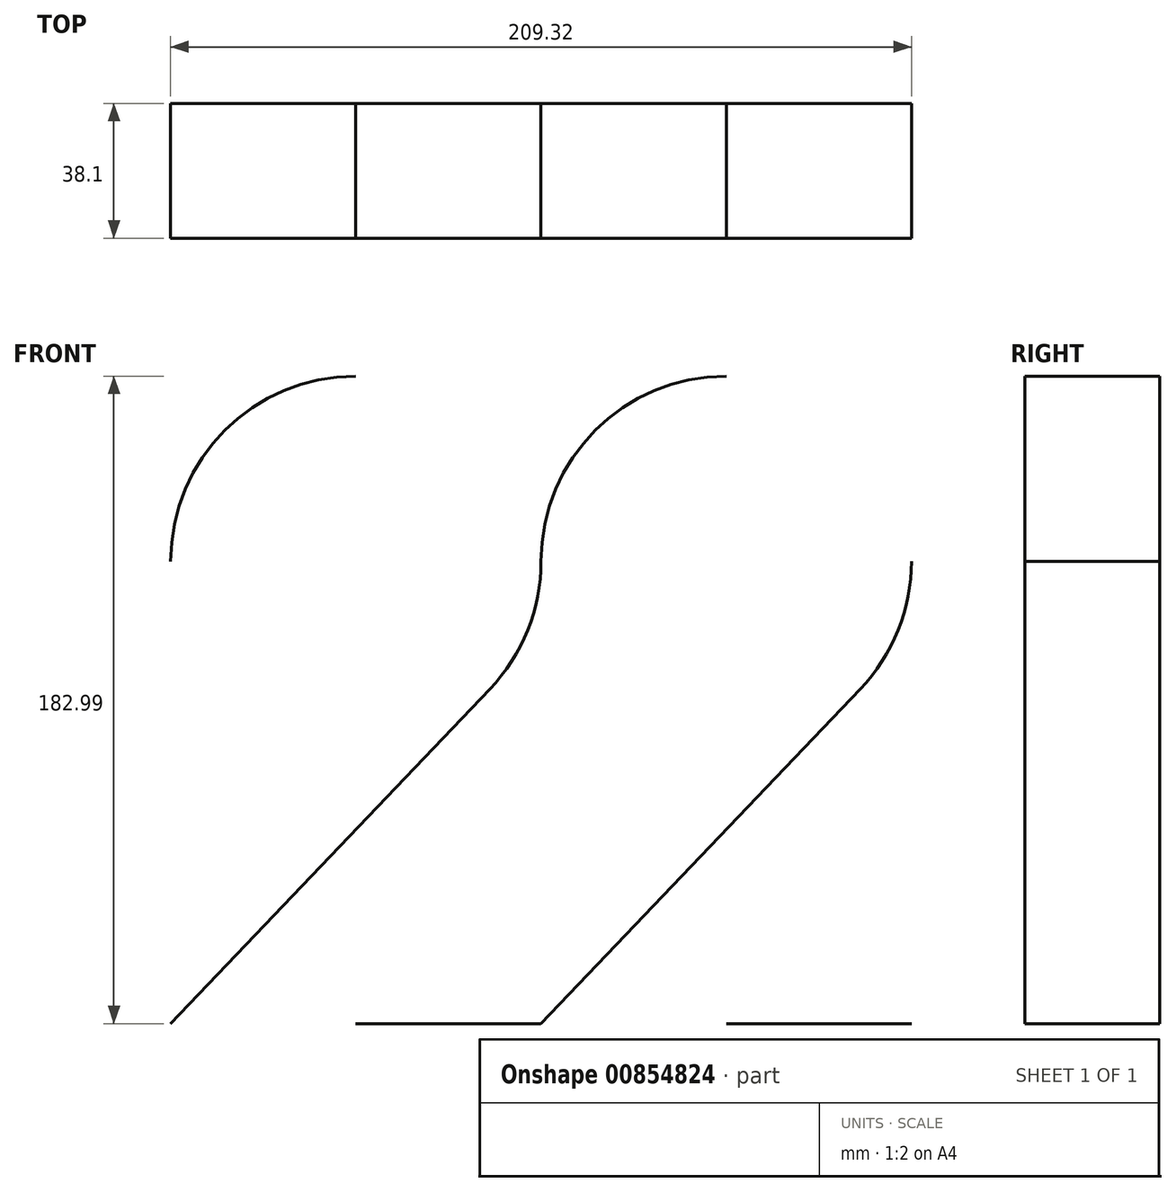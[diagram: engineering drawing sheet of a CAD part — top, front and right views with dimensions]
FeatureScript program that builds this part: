
annotation { "Feature Type Name" : "Feature", "Feature Type Description" : "" }
export const myFeature = defineFeature(function(context is Context, id is Id, definition is map)
    precondition{}
    {
        {
            var Q0;
            Q0=qCreatedBy(makeId("Front.planeOp"),FACE);
            var sketch = newSketch(context, id + "F0", { "sketchPlane" : qUnion([Q0])});
            skArc(sketch, "E0", {"start": v(37.86, -36.12) * mm, "mid": v(48.58, -19.46) * mm, "end": v(52.33, 0) * mm});
            skLineSegment(sketch, "E1", {"start": v(37.86, -36.12) * mm, "end": v(-52.33, -130.66) * mm});
            skLineSegment(sketch, "E2", {"start": v(0, -130.66) * mm, "end": v(52.33, -130.66) * mm});
            skLineSegment(sketch, "E3", {"start": v(-61.17, 0) * mm, "end": v(181.22, 0) * mm, "construction": true});
            skLineSegment(sketch, "E4", {"start": v(0, 77.41) * mm, "end": v(0, -140.2) * mm, "construction": true});
            skArc(sketch, "E5.trimOffspring", {"start": v(0, 52.33) * mm, "mid": v(-37, 37) * mm, "end": v(-52.33, 0) * mm});
            skLineSegment(sketch, "E6", {"start": v(52.33, -130.66) * mm, "end": v(142.52, -36.12) * mm});
            skLineSegment(sketch, "E7", {"start": v(37.86, -36.12) * mm, "end": v(142.52, -36.12) * mm, "construction": true});
            skLineSegment(sketch, "E8", {"start": v(0, 52.33) * mm, "end": v(184.25, 52.33) * mm, "construction": true});
            skArc(sketch, "E9", {"start": v(104.66, 52.33) * mm, "mid": v(67.66, 37) * mm, "end": v(52.33, 0) * mm});
            skPoint(sketch, "E9.third.point", {"position": v(104.66, 52.33) * mm});
            skLineSegment(sketch, "E10", {"start": v(104.66, 52.33) * mm, "end": v(104.66, -148.45) * mm, "construction": true});
            skLineSegment(sketch, "E11", {"start": v(104.66, -130.66) * mm, "end": v(156.99, -130.66) * mm});
            skArc(sketch, "E12.trimOffspring", {"start": v(142.52, -36.12) * mm, "mid": v(153.24, -19.46) * mm, "end": v(156.99, 0) * mm});
            skSolve(sketch);
        }
        {
            var Q0;
            Q0 = qBodyType(qCreatedBy(id + "F0" ,EDGE), BodyType.WIRE);
            extrude(context, id + "F1", {"bodyType" : ToolBodyType.SURFACE, "surfaceEntities" : qUnion([Q0]), "depth" : 38.1 * mm, "offsetDistance" : 25.4 * mm});
        }
    });
